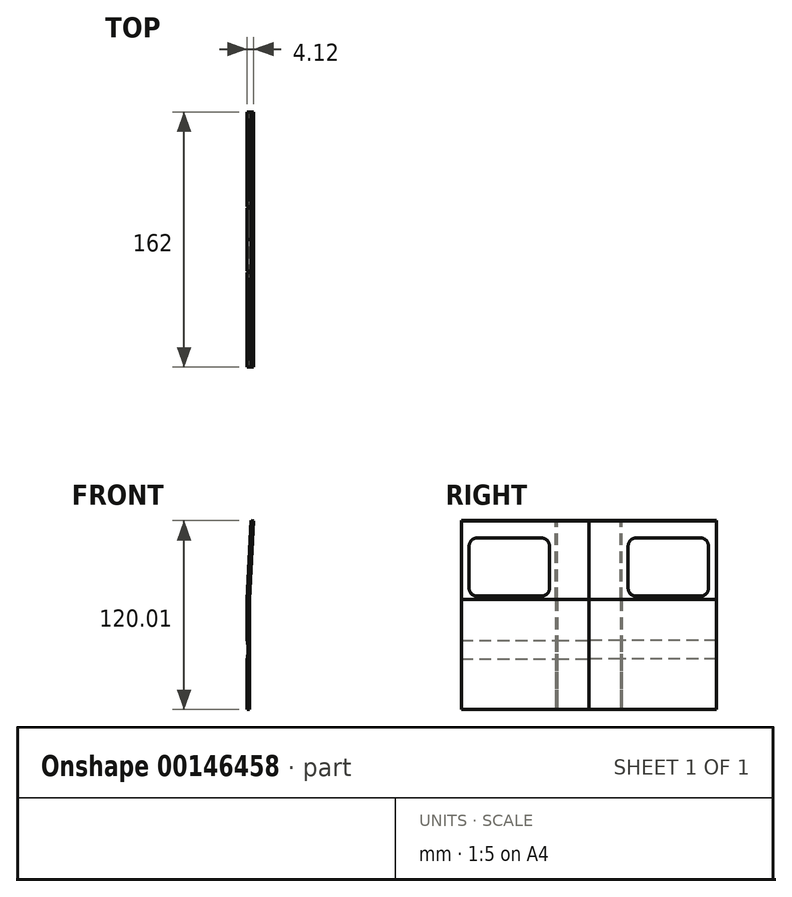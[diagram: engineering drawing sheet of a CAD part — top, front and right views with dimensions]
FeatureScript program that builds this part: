
annotation { "Feature Type Name" : "Feature", "Feature Type Description" : "" }
export const myFeature = defineFeature(function(context is Context, id is Id, definition is map)
    precondition{}
    {
        {
            var Q0;
            Q0=qCreatedBy(makeId("Front.planeOp"),FACE);
            var sketch = newSketch(context, id + "F0", { "sketchPlane" : qUnion([Q0])});
            skLineSegment(sketch, "E0", {"start": v(0, 0) * mm, "end": v(0, 70) * mm});
            skLineSegment(sketch, "E1", {"start": v(0, 70) * mm, "end": v(2.62, 120) * mm});
            skLineSegment(sketch, "E2", {"start": v(2.62, 120) * mm, "end": v(4.12, 119.93) * mm});
            skLineSegment(sketch, "E3", {"start": v(4.12, 119.93) * mm, "end": v(1.5, 70) * mm});
            skLineSegment(sketch, "E4", {"start": v(1.5, 70) * mm, "end": v(1.5, 0) * mm});
            skLineSegment(sketch, "E5", {"start": v(1.5, 0) * mm, "end": v(0, 0) * mm});
            skSolve(sketch);
        }
        {
            var Q0;
            Q0 = qSketchRegion(id + "F0", true);
            extrude(context, id + "F1", {"entities" : qUnion([Q0]), "oppositeDirection" : true, "depth" : 81 * mm});
        }
        {
            var Q0;
            Q0=makeQuery(id+"F1.opExtrude","SWEPT_FACE",FACE,{"disambiguationData":[OSD([sQuery(id+"F0.wireOp",EDGE,"E3")])]});
            var sketch = newSketch(context, id + "F2", { "sketchPlane" : qUnion([Q0])});
            skLineSegment(sketch, "E6.bottom", {"start": v(30, 108.98) * mm, "end": v(71, 108.98) * mm});
            skLineSegment(sketch, "E6.top", {"start": v(30, 71.98) * mm, "end": v(71, 71.98) * mm});
            skLineSegment(sketch, "E6.left", {"start": v(25, 103.98) * mm, "end": v(25, 76.98) * mm});
            skLineSegment(sketch, "E6.right", {"start": v(76, 103.98) * mm, "end": v(76, 76.98) * mm});
            skPoint(sketch, "E7.visualSharp", {"position": v(76, 108.98) * mm});
            skArc(sketch, "E7.filletArc", {"start": v(76, 103.98) * mm, "mid": v(74.54, 107.52) * mm, "end": v(71, 108.98) * mm});
            skPoint(sketch, "E8.visualSharp", {"position": v(25, 108.98) * mm});
            skArc(sketch, "E8.filletArc", {"start": v(30, 108.98) * mm, "mid": v(26.46, 107.52) * mm, "end": v(25, 103.98) * mm});
            skPoint(sketch, "E9.visualSharp", {"position": v(25, 71.98) * mm});
            skArc(sketch, "E9.filletArc", {"start": v(25, 76.98) * mm, "mid": v(26.46, 73.45) * mm, "end": v(30, 71.98) * mm});
            skPoint(sketch, "E10.visualSharp", {"position": v(76, 71.98) * mm});
            skArc(sketch, "E10.filletArc", {"start": v(71, 71.98) * mm, "mid": v(74.54, 73.45) * mm, "end": v(76, 76.98) * mm});
            skSolve(sketch);
        }
        {
            var Q0;
            Q0 = qSketchRegion(id + "F2", true);
            extrude(context, id + "F3", {"entities" : qUnion([Q0]), "operationType" : NewBodyOperationType.REMOVE, "endBound" : BoundingType.THROUGH_ALL, "oppositeDirection" : true, "depth" : 25 * mm});
        }
        {
            var Q0;
            Q0=makeQuery(id+"F1.opExtrude","CAP_FACE",FACE,{"disambiguationData":[OSD([sQuery(id+"F0.wireOp",EDGE,"E0"),sQuery(id+"F0.wireOp",EDGE,"E1"),sQuery(id+"F0.wireOp",EDGE,"E2"),sQuery(id+"F0.wireOp",EDGE,"E3"),sQuery(id+"F0.wireOp",EDGE,"E4"),sQuery(id+"F0.wireOp",EDGE,"E5")])],"isStart":true});
            var sketch = newSketch(context, id + "F4", { "sketchPlane" : qUnion([Q0])});
            skLineSegment(sketch, "E11", {"start": v(0, 44) * mm, "end": v(0, 32) * mm});
            skArc(sketch, "E12", {"start": v(0, 32) * mm, "mid": v(0.6, 38) * mm, "end": v(0, 44) * mm});
            skSolve(sketch);
        }
        {
            var Q0;
            Q0 = qSketchRegion(id + "F4", true);
            extrude(context, id + "F5", {"entities" : qUnion([Q0]), "operationType" : NewBodyOperationType.REMOVE, "endBound" : BoundingType.THROUGH_ALL, "oppositeDirection" : true, "depth" : 25 * mm});
        }
        {
            var Q0;
            {var subQ4=sQuery(id+"F0.wireOp",EDGE,"E1");var subQ5=sQuery(id+"F0.wireOp",EDGE,"E0");Q0=makeQuery(id+"F5.boolean.opBoolean","SPLIT",FACE,{"disambiguationData":[TD([makeQuery(id+"F1.opExtrude","SWEPT_FACE",FACE,{"disambiguationData":[OSD([subQ4])]})])],"derivedFrom":makeQuery(id+"F1.opExtrude","SWEPT_FACE",FACE,{"disambiguationData":[OSD([subQ5])]})});}
            var sketch = newSketch(context, id + "F6", { "sketchPlane" : qUnion([Q0])});
            skLineSegment(sketch, "E13.bottom", {"start": v(-21, 70) * mm, "end": v(-20, 70) * mm});
            skLineSegment(sketch, "E13.top", {"start": v(-21, 0) * mm, "end": v(-20, 0) * mm});
            skLineSegment(sketch, "E13.left", {"start": v(-21, 70) * mm, "end": v(-21, 0) * mm});
            skLineSegment(sketch, "E13.right", {"start": v(-20, 70) * mm, "end": v(-20, 0) * mm});
            skSolve(sketch);
        }
        {
            var Q0;
            Q0 = qSketchRegion(id + "F6", true);
            extrude(context, id + "F7", {"entities" : qUnion([Q0]), "operationType" : NewBodyOperationType.REMOVE, "oppositeDirection" : true, "depth" : 0.7 * mm});
        }
        {
            var Q0;
            Q0=makeQuery(id+"F1.opExtrude","SWEPT_FACE",FACE,{"disambiguationData":[OSD([sQuery(id+"F0.wireOp",EDGE,"E1")])]});
            var sketch = newSketch(context, id + "F8", { "sketchPlane" : qUnion([Q0])});
            skLineSegment(sketch, "E14.bottom", {"start": v(-20, 69.9) * mm, "end": v(-21, 69.9) * mm});
            skLineSegment(sketch, "E14.top", {"start": v(-20, 119.98) * mm, "end": v(-21, 119.98) * mm});
            skLineSegment(sketch, "E14.left", {"start": v(-20, 69.9) * mm, "end": v(-20, 119.98) * mm});
            skLineSegment(sketch, "E14.right", {"start": v(-21, 69.9) * mm, "end": v(-21, 119.98) * mm});
            skSolve(sketch);
        }
        {
            var Q0;
            Q0 = qSketchRegion(id + "F8", true);
            extrude(context, id + "F9", {"entities" : qUnion([Q0]), "operationType" : NewBodyOperationType.REMOVE, "oppositeDirection" : true, "depth" : 0.7 * mm});
        }
        {
            var Q0;
            Q0=makeQuery(id+"F1.opExtrude","SWEPT_BODY",BODY,{"disambiguationData":[OSD([sQuery(id+"F0.wireOp",EDGE,"E0"),sQuery(id+"F0.wireOp",EDGE,"E1"),sQuery(id+"F0.wireOp",EDGE,"E2"),sQuery(id+"F0.wireOp",EDGE,"E3"),sQuery(id+"F0.wireOp",EDGE,"E4"),sQuery(id+"F0.wireOp",EDGE,"E5")])]});
            var Q1;
            Q1=qCreatedBy(makeId("Front.planeOp"),FACE);
            mirror(context, id + "F10", {"entities" : qUnion([Q0]), "mirrorPlane" : qUnion([Q1])});
        }
    });
